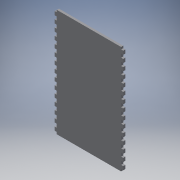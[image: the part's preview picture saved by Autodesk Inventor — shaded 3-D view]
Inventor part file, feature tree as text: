
AUTODESK INVENTOR PART (.ipt)
format: ipt  version: 2019 (Build 230136000, 136)  size: 218,624 bytes
history: native  units: mm
features: reference x35, other x4, extrude x1, sketch x1
ambient origin geometry x8: Origin, YZ Plane, XZ Plane, XY Plane, X Axis, Y Axis, Z Axis, Center Point
bodies: Body1 (feature_tree)
feature tree (41):
  other  "Твердое тело1"
  extrude  "Выдавливание1"  Depth=6.0mm TaperAngle=0.0deg
  sketch  "Эскиз1"
  reference  "Ссылка1"
  reference  "Ссылка2"
  reference  "Ссылка3"
  reference  "Ссылка4"
  reference  "Ссылка5"
  reference  "Ссылка6"
  reference  "Ссылка7"
  reference  "Ссылка8"
  reference  "Ссылка9"
  reference  "Ссылка10"
  reference  "Ссылка11"
  reference  "Ссылка12"
  reference  "Ссылка13"
  reference  "Ссылка14"
  reference  "Ссылка15"
  reference  "Ссылка16"
  reference  "Ссылка17"
  reference  "Ссылка18"
  reference  "Ссылка19"
  reference  "Ссылка20"
  reference  "Ссылка21"
  reference  "Ссылка22"
  reference  "Ссылка23"
  reference  "Ссылка24"
  reference  "Ссылка25"
  reference  "Ссылка26"
  reference  "Ссылка27"
  reference  "Ссылка28"
  reference  "Ссылка29"
  reference  "Ссылка30"
  reference  "Ссылка31"
  reference  "Ссылка32"
  reference  "Ссылка33"
  reference  "Ссылка34"
  reference  "Ссылка35"
  other  "Сборка2"
  other  "боковина:2"
  other  "боковина:1"
